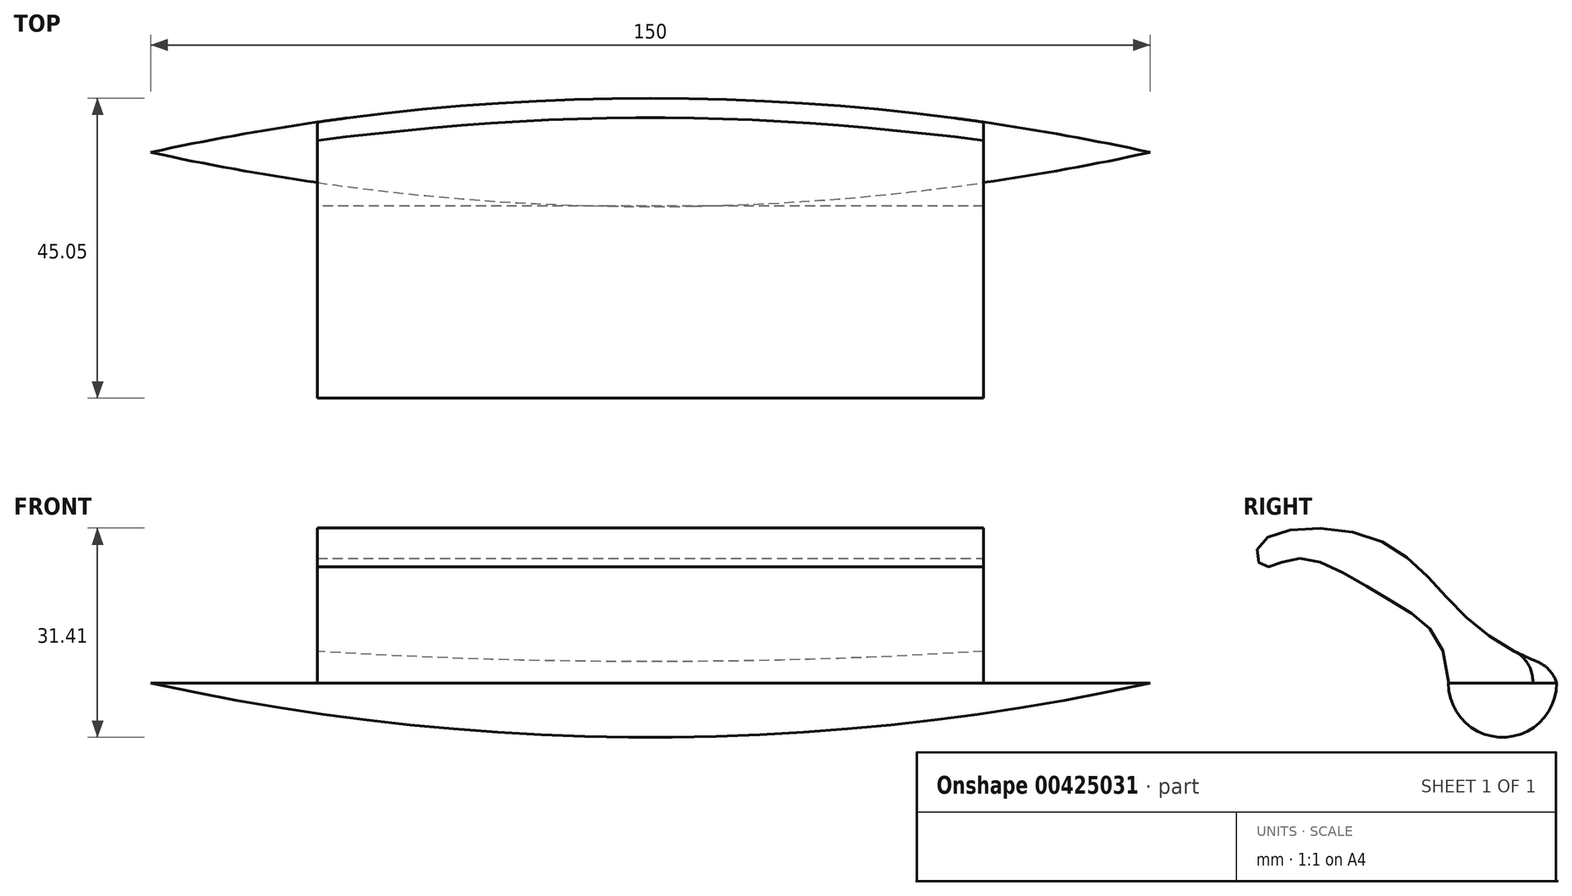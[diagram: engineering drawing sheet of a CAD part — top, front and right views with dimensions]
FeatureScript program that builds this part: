
annotation { "Feature Type Name" : "Feature", "Feature Type Description" : "" }
export const myFeature = defineFeature(function(context is Context, id is Id, definition is map)
    precondition{}
    {
        {
            var Q0;
            Q0=qCreatedBy(makeId("Front.planeOp"),FACE);
            var sketch = newSketch(context, id + "F0", { "sketchPlane" : qUnion([Q0])});
            skLineSegment(sketch, "E0", {"start": v(-75, 0) * mm, "end": v(75, 0) * mm});
            skArc(sketch, "E1", {"start": v(-75, 0) * mm, "mid": v(0, -8.13) * mm, "end": v(75, 0) * mm});
            skSolve(sketch);
        }
        {
            var Q0;
            Q0=makeQuery(id+"F0.imprint","IMPRINT",FACE,{"disambiguationData":[TD([[makeQuery(id+"F0.imprint","IMPRINT",EDGE,{"derivedFrom":sQuery(id+"F0.wireOp",EDGE,"E0")}),-1.0]])]});
            var Q1;
            Q1=sQuery(id+"F0.wireOp",EDGE,"E0");
            revolve(context, id + "F1", {"entities" : qUnion([Q0]), "axis" : qUnion([Q1]), "revolveType" : RevolveType.SYMMETRIC, "angle" : 180 * degree});
        }
        {
            var Q0;
            Q0=qCreatedBy(makeId("Right.planeOp"),FACE);
            var sketch = newSketch(context, id + "F2", { "sketchPlane" : qUnion([Q0])});
            skFitSpline(sketch, "E2", {"points": [v(17.9, 0) * mm, v(-4.33, 8.89) * mm, v(-19.09, 21.65) * mm, v(-36.45, 20.9) * mm, v(-35.95, 17.55) * mm, v(-30.75, 18.73) * mm, v(-17.3, 12.67) * mm, v(-8.07, 0) * mm], "startDerivative": vector(-138.55, 18.6) * mm, "endDerivative": vector(7.4, -156.35) * mm});
            skLineSegment(sketch, "E3", {"start": v(-8.07, 0) * mm, "end": v(17.9, 0) * mm});
            skSolve(sketch);
        }
        {
            var Q0;
            Q0=makeQuery(id+"F2.imprint","IMPRINT",FACE,{"disambiguationData":[TD([[makeQuery(id+"F2.imprint","IMPRINT",EDGE,{"derivedFrom":sQuery(id+"F2.wireOp",EDGE,"E2")}),1.0]])]});
            extrude(context, id + "F3", {"entities" : qUnion([Q0]), "operationType" : NewBodyOperationType.ADD, "endBound" : BoundingType.SYMMETRIC, "depth" : 100 * mm});
        }
        {
            var Q0;
            {var subQ0=sQuery(id+"F2.wireOp",EDGE,"E3");var subQ1=sQuery(id+"F2.wireOp",EDGE,"E2");Q0=makeQuery(id+"F3.opExtrude","SWEPT_EDGE",EDGE,{"disambiguationData":[OSD([subQ1,subQ0]),TDD([makeQuery(id+"F2.imprint","INTERSECT",VERTEX,{"disambiguationData":[OD(0.0)],"derivedFrom":[subQ1,subQ0]})])]});}
            fillet(context, id + "F4", {"entities" : qUnion([Q0]), "radius" : 5 * mm, "tangentPropagation" : true, "allowEdgeOverflow" : false});
        }
    });
